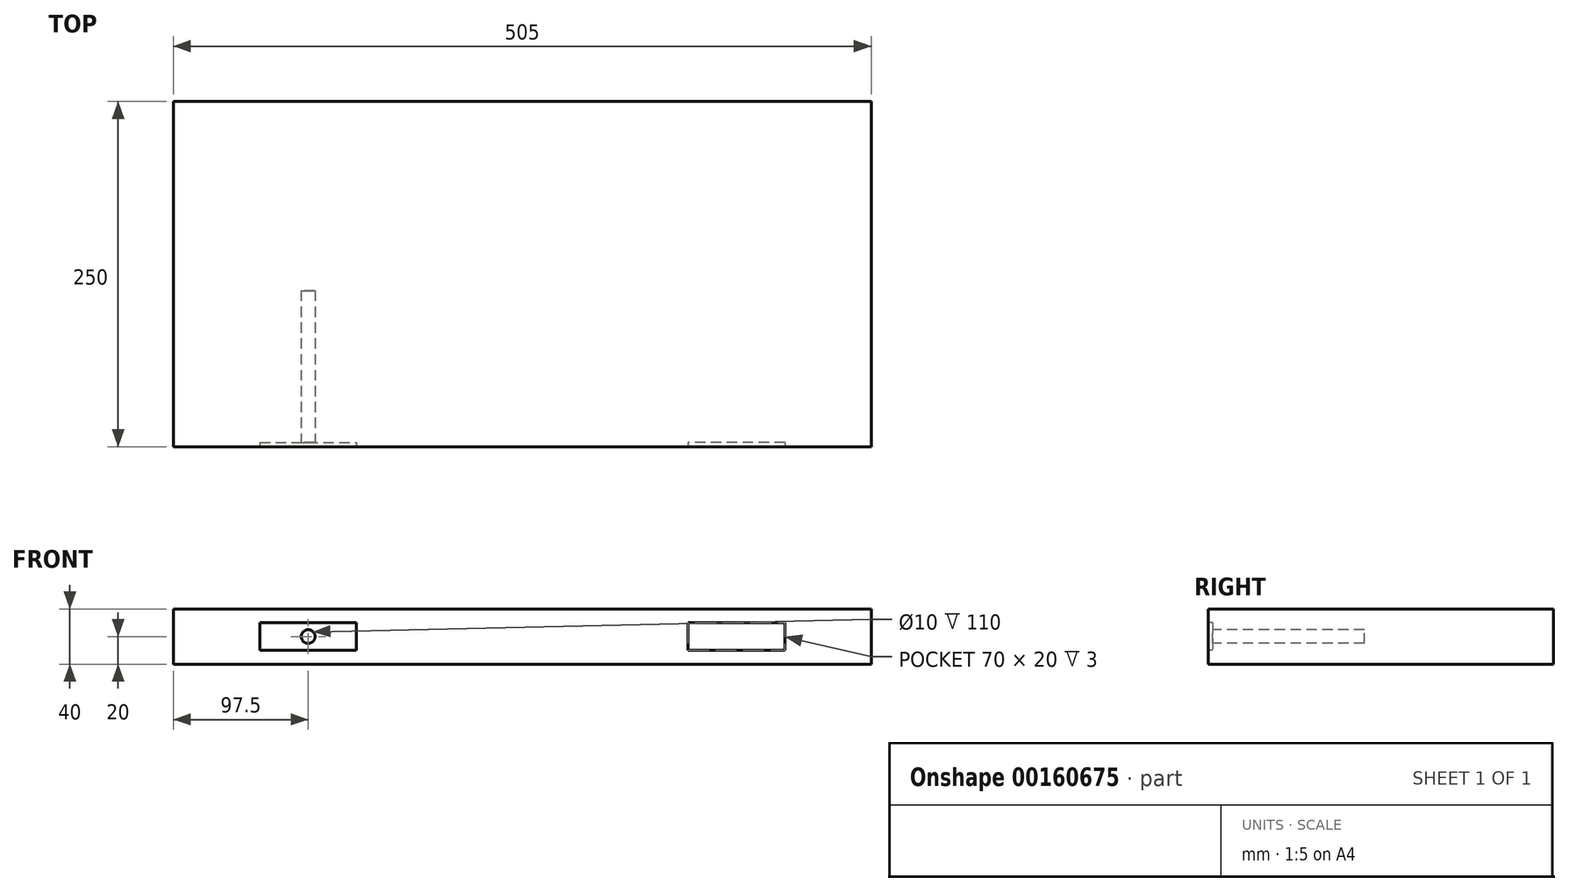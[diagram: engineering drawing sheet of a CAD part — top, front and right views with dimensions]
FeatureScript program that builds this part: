
annotation { "Feature Type Name" : "Feature", "Feature Type Description" : "" }
export const myFeature = defineFeature(function(context is Context, id is Id, definition is map)
    precondition{}
    {
        {
            var Q0;
            Q0=qCreatedBy(makeId("Top.planeOp"),FACE);
            var sketch = newSketch(context, id + "F0", { "sketchPlane" : qUnion([Q0])});
            skLineSegment(sketch, "E0.bottom", {"start": v(-252.5, 125) * mm, "end": v(252.5, 125) * mm});
            skLineSegment(sketch, "E0.top", {"start": v(-252.5, -125) * mm, "end": v(252.5, -125) * mm});
            skLineSegment(sketch, "E0.left", {"start": v(-252.5, 125) * mm, "end": v(-252.5, -125) * mm});
            skLineSegment(sketch, "E0.right", {"start": v(252.5, 125) * mm, "end": v(252.5, -125) * mm});
            skSolve(sketch);
        }
        {
            var Q0;
            Q0=makeQuery(id+"F0.imprint","IMPRINT",FACE,{"disambiguationData":[TD([[makeQuery(id+"F0.imprint","IMPRINT",EDGE,{"derivedFrom":sQuery(id+"F0.wireOp",EDGE,"E0.bottom")}),-1.0]])]});
            extrude(context, id + "F1", {"entities" : qUnion([Q0]), "depth" : 40 * mm});
        }
        {
            var Q0;
            Q0=makeQuery(id+"F1.opExtrude","SWEPT_FACE",FACE,{"disambiguationData":[OSD([sQuery(id+"F0.wireOp",EDGE,"E0.top")])]});
            var sketch = newSketch(context, id + "F2", { "sketchPlane" : qUnion([Q0])});
            skLineSegment(sketch, "E1.bottom", {"start": v(190, 30) * mm, "end": v(120, 30) * mm});
            skLineSegment(sketch, "E1.top", {"start": v(190, 10) * mm, "end": v(120, 10) * mm});
            skLineSegment(sketch, "E1.left", {"start": v(190, 30) * mm, "end": v(190, 10) * mm});
            skLineSegment(sketch, "E1.right", {"start": v(120, 30) * mm, "end": v(120, 10) * mm});
            skLineSegment(sketch, "E2", {"start": v(155, 48.65) * mm, "end": v(155, -20.15) * mm, "construction": true});
            skLineSegment(sketch, "E3.MirrorCS", {"start": v(-190, 30) * mm, "end": v(-120, 30) * mm});
            skLineSegment(sketch, "E4.MirrorCS", {"start": v(-120, 30) * mm, "end": v(-120, 10) * mm});
            skLineSegment(sketch, "E5.MirrorCS", {"start": v(-190, 10) * mm, "end": v(-120, 10) * mm});
            skLineSegment(sketch, "E6.MirrorCS", {"start": v(-190, 30) * mm, "end": v(-190, 10) * mm});
            skSolve(sketch);
        }
        {
            var Q0;
            Q0=makeQuery(id+"F2.imprint","IMPRINT",FACE,{"disambiguationData":[TD([[makeQuery(id+"F2.imprint","IMPRINT",EDGE,{"derivedFrom":sQuery(id+"F2.wireOp",EDGE,"E1.bottom")}),1.0]])]});
            var Q1;
            Q1=makeQuery(id+"F2.imprint","IMPRINT",FACE,{"disambiguationData":[TD([[makeQuery(id+"F2.imprint","IMPRINT",EDGE,{"derivedFrom":sQuery(id+"F2.wireOp",EDGE,"E3.MirrorCS")}),-1.0]])]});
            extrude(context, id + "F3", {"entities" : qUnion([Q0, Q1]), "operationType" : NewBodyOperationType.REMOVE, "oppositeDirection" : true, "depth" : 3 * mm});
        }
        {
            var Q0;
            Q0=makeQuery(id+"F3.boolean.opBoolean","COPY",FACE,{"derivedFrom":makeQuery(id+"F3.opExtrude","CAP_FACE",FACE,{"disambiguationData":[OSD([sQuery(id+"F2.wireOp",EDGE,"E3.MirrorCS"),sQuery(id+"F2.wireOp",EDGE,"E4.MirrorCS"),sQuery(id+"F2.wireOp",EDGE,"E5.MirrorCS"),sQuery(id+"F2.wireOp",EDGE,"E6.MirrorCS")])],"isStart":false})});
            var sketch = newSketch(context, id + "F4", { "sketchPlane" : qUnion([Q0])});
            skCircle(sketch, "E7", {"center": v(-155, 20) * mm, "radius": 5 * mm});
            skPoint(sketch, "E7.centerSnap0", {"position": v(-190, 20) * mm});
            skPoint(sketch, "E7.centerSnap1", {"position": v(-155, 30) * mm});
            skCircle(sketch, "E8.MirrorC", {"center": v(155, 20) * mm, "radius": 5 * mm});
            skSolve(sketch);
        }
        {
            var Q0;
            Q0=makeQuery(id+"F4.imprint","IMPRINT",FACE,{"disambiguationData":[TD([[makeQuery(id+"F4.imprint","IMPRINT",EDGE,{"derivedFrom":sQuery(id+"F4.wireOp",EDGE,"E7")}),1.0]])]});
            var Q1;
            Q1=makeQuery(id+"F4.imprint","IMPRINT",FACE,{"disambiguationData":[TD([[makeQuery(id+"F4.imprint","IMPRINT",EDGE,{"derivedFrom":sQuery(id+"F4.wireOp",EDGE,"E8.MirrorC")}),-1.0]])]});
            extrude(context, id + "F5", {"entities" : qUnion([Q0, Q1]), "operationType" : NewBodyOperationType.REMOVE, "oppositeDirection" : true, "depth" : 110 * mm});
        }
    });
